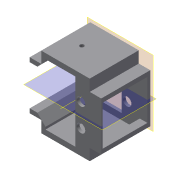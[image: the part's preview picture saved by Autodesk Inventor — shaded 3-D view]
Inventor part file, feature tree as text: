
AUTODESK INVENTOR PART (.ipt)
format: ipt  version: 2019.4 (Build 234330000, 330)  size: 312,320 bytes
history: native  units: mm
features: other x14, reference x11, projected_geometry x6, plane x5, extrude x5, sketch x4, chamfer x1, pattern_circular x1, mirror x1
ambient origin geometry x8: Origin, YZ Plane, XZ Plane, XY Plane, X Axis, Y Axis, Z Axis, Center Point
bodies: Solid1 (feature_tree)
feature tree (48):
  plane  "Work Plane1"
  extrude  "Extrusion1"  Depth=0.1mm
  chamfer  "Chamfer1"  [1 undecoded]
  sketch  "Sketch2"  dims[d3=0.1mm]
  plane  "Work Plane2"
  extrude  "Extrusion2"  TaperAngle=0.0deg  [1 undecoded]
  other  "Work Axis1"
  pattern_circular  "Circular Pattern1"  [2 undecoded]
  extrude  "Extrusion3"  Depth=2.0mm TaperAngle=45.0deg
  plane  "Work Plane3"
  plane  "Work Plane4"
  other  "Work Point1"
  extrude  "Extrusion12"  Depth=3.001102mm
  plane  "Work Plane5"
  mirror  "Mirror1"
  extrude  "Extrusion14"  Depth=2.0mm TaperAngle=0.0deg
  sketch  "Sketch1"  dims[d1=0.1mm d2=0.1mm]
  reference  "Reference1"
  reference  "Reference2"
  reference  "Reference3"
  reference  "Reference4"
  reference  "Reference5"
  reference  "Reference6"
  reference  "Reference7"
  projected_geometry  "Projected Loop1"
  sketch  "Sketch3"  dims[d4=0.1mm]
  reference  "Reference8"
  projected_geometry  "Projected Loop2"
  projected_geometry  "Projected Loop3"
  projected_geometry  "Projected Loop8"
  reference  "Reference28"
  reference  "Reference31"
  reference  "Reference32"
  sketch  "Sketch16"  dims[d5=0.1mm d6=0.0mm d7=0.0mm d8=2.0mm d9=0.0mm d10=3.9mm d11=2.0mm d12=45.0deg d13=3.001102mm d14=6.0mm d15=0.0mm d16=40.0mm d17=360.0deg d19=6.0mm d20=1.0mm d21=0.0mm d82=10.0mm d83=0.0mm d89=2.8mm d90=10.0mm d91=33.74mm d95=2.0mm d96=0.0mm]
  projected_geometry  "Projected Loop10"
  projected_geometry  "Projected Loop11"
  other  "Assembly_Cube_Z_Focus_MGN_NEMA_v3.iam"
  other  "00_MGN12 LINEAR GUIDE RAIL, CONFIGURABLE:1"
  other  "Assembly_Cube_Z_Focus_MGN_manual_v3.iam"
  other  "Assembly_Cube_empty_IM_v3:1"
  other  "10_Cube_1x1_IM:2"
  other  "10_Cube_1x1_IM:1"
  other  "00_NEMA11:1"
  other  "DIN 912 - replaced by DIN EN ISO 4762 M3 x 30:1"
  other  "30_Cube_Z_Focus_MGN12_manual_gear_v3:1"
  other  "Assembly_Cube_Z_Focus_Drylin_manual_v3.iam"
  other  "00_rod_6mm:3"
  other  "00_rod_6mm:2"
note: 4 required parameter values undecoded (feature->parameter linkage not recoverable at this tier; creation-order binding heuristic only, values carry confidence <= 0.55)
